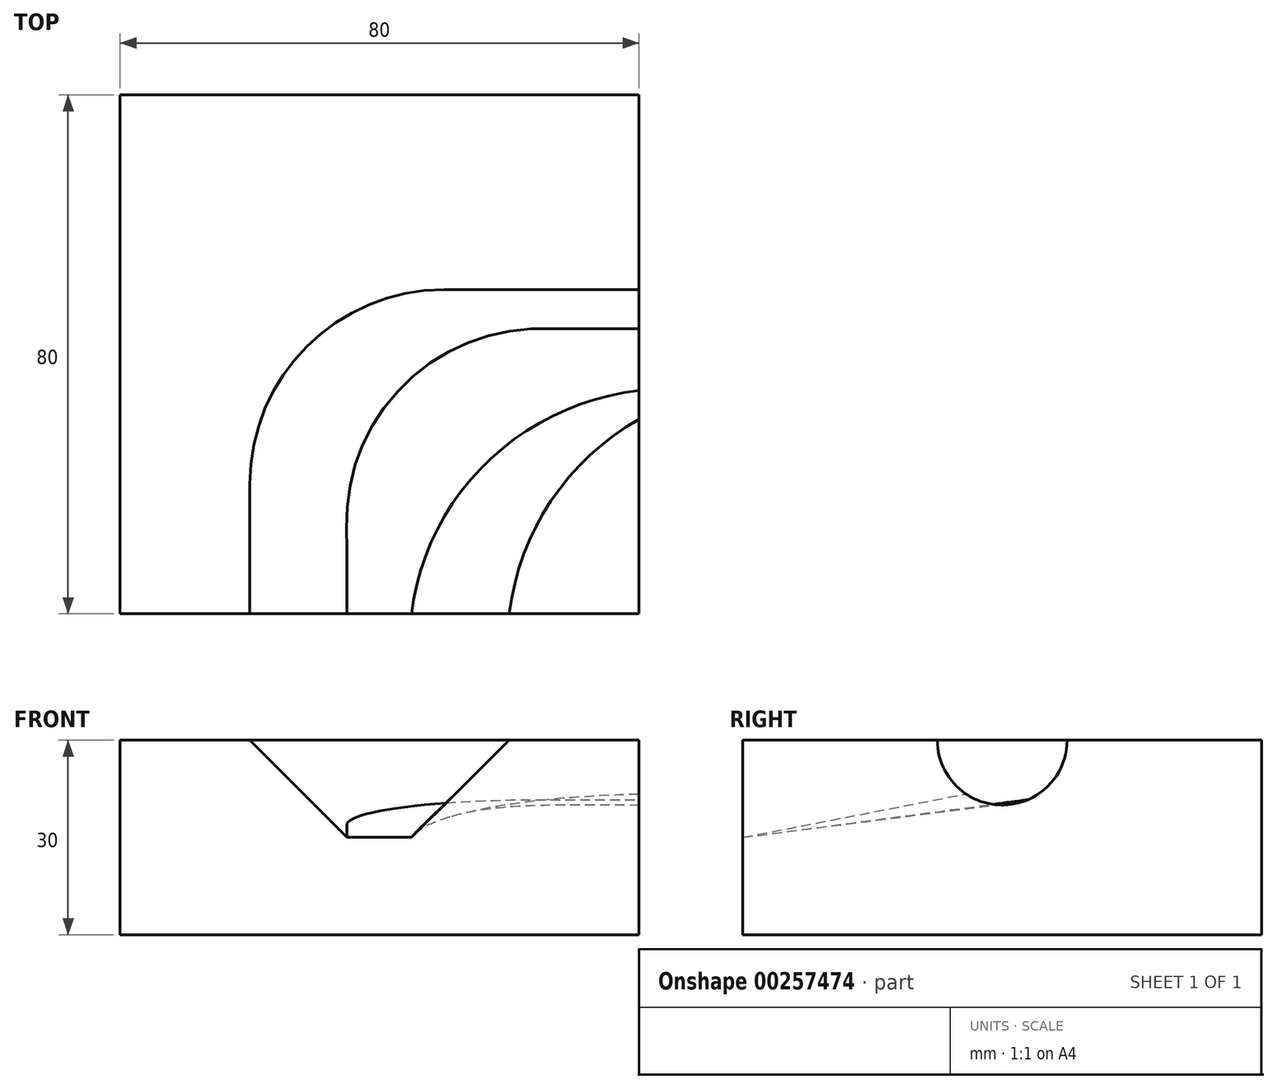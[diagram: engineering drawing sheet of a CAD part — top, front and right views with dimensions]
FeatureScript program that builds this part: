
annotation { "Feature Type Name" : "Feature", "Feature Type Description" : "" }
export const myFeature = defineFeature(function(context is Context, id is Id, definition is map)
    precondition{}
    {
        {
            var Q0;
            Q0=qCreatedBy(makeId("Top.planeOp"),FACE);
            var sketch = newSketch(context, id + "F0", { "sketchPlane" : qUnion([Q0])});
            skLineSegment(sketch, "E0.bottom", {"start": v(-40, 40) * mm, "end": v(40, 40) * mm});
            skLineSegment(sketch, "E0.top", {"start": v(-40, -40) * mm, "end": v(40, -40) * mm});
            skLineSegment(sketch, "E0.left", {"start": v(-40, 40) * mm, "end": v(-40, -40) * mm});
            skLineSegment(sketch, "E0.right", {"start": v(40, 40) * mm, "end": v(40, -40) * mm});
            skPoint(sketch, "E0.middle", {"position": v(0, 0) * mm});
            skSolve(sketch);
        }
        {
            var Q0;
            Q0=makeQuery(id+"F0.imprint","IMPRINT",FACE,{"disambiguationData":[TD([[makeQuery(id+"F0.imprint","IMPRINT",EDGE,{"derivedFrom":sQuery(id+"F0.wireOp",EDGE,"E0.bottom")}),-1.0]])]});
            extrude(context, id + "F1", {"entities" : qUnion([Q0]), "depth" : 30 * mm});
        }
        {
            var Q0;
            Q0=makeQuery(id+"F1.opExtrude","SWEPT_FACE",FACE,{"disambiguationData":[OSD([sQuery(id+"F0.wireOp",EDGE,"E0.right")])]});
            var sketch = newSketch(context, id + "F2", { "sketchPlane" : qUnion([Q0])});
            skPoint(sketch, "E1", {"position": v(0, 30) * mm});
            skArc(sketch, "E2", {"start": v(-10, 30) * mm, "mid": v(0, 20) * mm, "end": v(10, 30) * mm});
            skLineSegment(sketch, "E3.0.0", {"start": v(-40, 0) * mm, "end": v(40, 0) * mm});
            skLineSegment(sketch, "E3.0.1", {"start": v(40, 0) * mm, "end": v(40, 30) * mm});
            skLineSegment(sketch, "E3.0.2", {"start": v(40, 30) * mm, "end": v(-40, 30) * mm});
            skLineSegment(sketch, "E3.0.3", {"start": v(-40, 30) * mm, "end": v(-40, 0) * mm});
            skLineSegment(sketch, "E4", {"start": v(-10.13, 22.13) * mm, "end": v(12.9, 20) * mm, "construction": true});
            skPoint(sketch, "E4.endSnap0", {"position": v(0, 20) * mm});
            skPoint(sketch, "E5", {"position": v(-5.6, 21.71) * mm});
            skPoint(sketch, "E6", {"position": v(3.98, 20.83) * mm});
            skSolve(sketch);
        }
        {
            var Q0;
            Q0=makeQuery(id+"F1.opExtrude","SWEPT_FACE",FACE,{"disambiguationData":[OSD([sQuery(id+"F0.wireOp",EDGE,"E0.top")])]});
            var sketch = newSketch(context, id + "F3", { "sketchPlane" : qUnion([Q0])});
            skPoint(sketch, "E7.startSnap0", {"position": v(-40, 15) * mm});
            skPoint(sketch, "E8", {"position": v(20, 30) * mm});
            skPoint(sketch, "E9", {"position": v(-20, 30) * mm});
            skLineSegment(sketch, "E10", {"start": v(-5.06, 15) * mm, "end": v(4.94, 15) * mm});
            skLineSegment(sketch, "E11", {"start": v(20, 30) * mm, "end": v(4.94, 15) * mm});
            skLineSegment(sketch, "E12", {"start": v(-20, 30) * mm, "end": v(-5.06, 15) * mm});
            skSolve(sketch);
        }
        {
            var Q0;
            Q0=makeQuery(id+"F1.opExtrude","CAP_FACE",FACE,{"disambiguationData":[OSD([sQuery(id+"F0.wireOp",EDGE,"E0.bottom"),sQuery(id+"F0.wireOp",EDGE,"E0.top"),sQuery(id+"F0.wireOp",EDGE,"E0.left"),sQuery(id+"F0.wireOp",EDGE,"E0.right")])],"isStart":false});
            var sketch = newSketch(context, id + "F4", { "sketchPlane" : qUnion([Q0])});
            skLineSegment(sketch, "E13.0.0", {"start": v(-40, 40) * mm, "end": v(-40, -40) * mm});
            skLineSegment(sketch, "E13.0.1", {"start": v(-40, -40) * mm, "end": v(40, -40) * mm});
            skLineSegment(sketch, "E13.0.2", {"start": v(40, -40) * mm, "end": v(40, 40) * mm});
            skLineSegment(sketch, "E13.0.3", {"start": v(40, 40) * mm, "end": v(-40, 40) * mm});
            skLineSegment(sketch, "E14", {"start": v(40, 10) * mm, "end": v(10, 10) * mm});
            skLineSegment(sketch, "E15", {"start": v(-20, -20) * mm, "end": v(-20, -40) * mm});
            skArc(sketch, "E16", {"start": v(40, -10) * mm, "mid": v(26.43, -22.62) * mm, "end": v(20, -40) * mm});
            skPoint(sketch, "E17.visualSharp", {"position": v(-20, 10) * mm});
            skArc(sketch, "E17.filletArc", {"start": v(10, 10) * mm, "mid": v(-11.21, 1.21) * mm, "end": v(-20, -20) * mm});
            skSolve(sketch);
        }
        {
            var Q0;
            Q0=qCreatedBy(makeId("Top.planeOp"),FACE);
            cPlane(context, id + "F5", {"entities" : qUnion([Q0]), "cplaneType" : CPlaneType.OFFSET, "offset" : 30 * mm, "width" : 150 * mm, "height" : 150 * mm});
        }
        {
            var Q0;
            Q0=qCreatedBy(id+"F5.planeOp",FACE);
            var sketch = newSketch(context, id + "F6", { "sketchPlane" : qUnion([Q0])});
            skLineSegment(sketch, "E18.0", {"start": v(40, 10) * mm, "end": v(10, 10) * mm});
            skArc(sketch, "E19.0", {"start": v(10, 10) * mm, "mid": v(-11.21, 1.21) * mm, "end": v(-20, -20) * mm});
            skLineSegment(sketch, "E20.0", {"start": v(-20, -20) * mm, "end": v(-20, -40) * mm});
            skSolve(sketch);
        }
        {
            var Q0;
            Q0=sQuery(id+"F3.wireOp",VERTEX,"E11.end");
            var Q1;
            Q1=sQuery(id+"F2.wireOp",VERTEX,"E5");
            var Q2;
            Q2=sQuery(id+"F3.wireOp",VERTEX,"E12.end");
            cPlane(context, id + "F7", {"entities" : qUnion([Q0, Q1, Q2]), "cplaneType" : CPlaneType.THREE_POINT, "offset" : 25 * mm, "width" : 150 * mm, "height" : 150 * mm});
        }
        {
            var Q0;
            Q0=qCreatedBy(id+"F7.planeOp",FACE);
            var sketch = newSketch(context, id + "F8", { "sketchPlane" : qUnion([Q0])});
            skPoint(sketch, "E21.0", {"position": v(4.94, 36.39) * mm});
            skPoint(sketch, "E22.0", {"position": v(40, 1.33) * mm});
            skArc(sketch, "E23", {"start": v(4.94, 36.39) * mm, "mid": v(16.38, 12.77) * mm, "end": v(40, 1.33) * mm});
            skSolve(sketch);
        }
        {
            var Q0;
            Q0=sQuery(id+"F3.wireOp",VERTEX,"E12.end");
            var Q1;
            Q1=sQuery(id+"F2.wireOp",VERTEX,"E6");
            var Q2;
            Q2=sQuery(id+"F8.wireOp",VERTEX,"E21.0");
            cPlane(context, id + "F9", {"entities" : qUnion([Q0, Q1, Q2]), "cplaneType" : CPlaneType.THREE_POINT, "offset" : 25 * mm, "width" : 150 * mm, "height" : 150 * mm});
        }
        {
            var Q0;
            Q0=qCreatedBy(id+"F9.planeOp",FACE);
            var sketch = newSketch(context, id + "F10", { "sketchPlane" : qUnion([Q0])});
            skPoint(sketch, "E24.0", {"position": v(-5.06, -37.68) * mm});
            skPoint(sketch, "E25.0", {"position": v(40, 6.68) * mm});
            skLineSegment(sketch, "E26", {"start": v(-5.06, -37.68) * mm, "end": v(-5.06, -23.32) * mm});
            skLineSegment(sketch, "E27", {"start": v(24.94, 6.68) * mm, "end": v(40, 6.68) * mm});
            skPoint(sketch, "E28.visualSharp", {"position": v(-5.06, 6.68) * mm});
            skArc(sketch, "E28.filletArc", {"start": v(24.94, 6.68) * mm, "mid": v(3.72, -2.1) * mm, "end": v(-5.06, -23.32) * mm});
            skSolve(sketch);
        }
        {
            var Q1;
            Q1=makeQuery(id+"F3.imprint","IMPRINT",FACE,{"disambiguationData":[TD([[makeQuery(id+"F3.imprint","IMPRINT",EDGE,{"derivedFrom":sQuery(id+"F3.wireOp",EDGE,"E10")}),1.0]])]});
            var Q2;
            {var subQ0=sQuery(id+"F2.wireOp",EDGE,"E2");Q2=makeQuery(id+"F2.imprint","IMPRINT",FACE,{"disambiguationData":[TD([[makeQuery(id+"F2.imprint","IMPRINT",EDGE,{"derivedFrom":subQ0}),1.0]])]});}
            var Q3;
            Q3=sQuery(id+"F4.wireOp",EDGE,"E16");
            var Q4;
            Q4 = qConstructionFilter(qBodyType(qCreatedBy(id + "F6" ,EDGE), BodyType.WIRE), ConstructionObject.NO);
            var Q5;
            Q5 = qConstructionFilter(qBodyType(qCreatedBy(id + "F8" ,EDGE), BodyType.WIRE), ConstructionObject.NO);
            var Q6;
            Q6 = qConstructionFilter(qBodyType(qCreatedBy(id + "F10" ,EDGE), BodyType.WIRE), ConstructionObject.NO);
            loft(context, id + "F11", {"operationType" : NewBodyOperationType.REMOVE, "addGuides" : true, "sheetProfilesArray" : [{ "sheetProfileEntities" : qUnion([Q1]) }, { "sheetProfileEntities" : qUnion([Q2]) }], "guidesArray" : [{ "guideEntities" : qUnion([Q3]), "guideDerivativeType" : LoftGuideDerivativeType.DEFAULT, "guideDerivativeMagnitude" : 1 }, { "guideEntities" : qUnion([Q4]), "guideDerivativeType" : LoftGuideDerivativeType.DEFAULT, "guideDerivativeMagnitude" : 1 }, { "guideEntities" : qUnion([Q5]), "guideDerivativeType" : LoftGuideDerivativeType.DEFAULT, "guideDerivativeMagnitude" : 1 }, { "guideEntities" : qUnion([Q6]), "guideDerivativeType" : LoftGuideDerivativeType.DEFAULT, "guideDerivativeMagnitude" : 1 }]});
        }
    });
